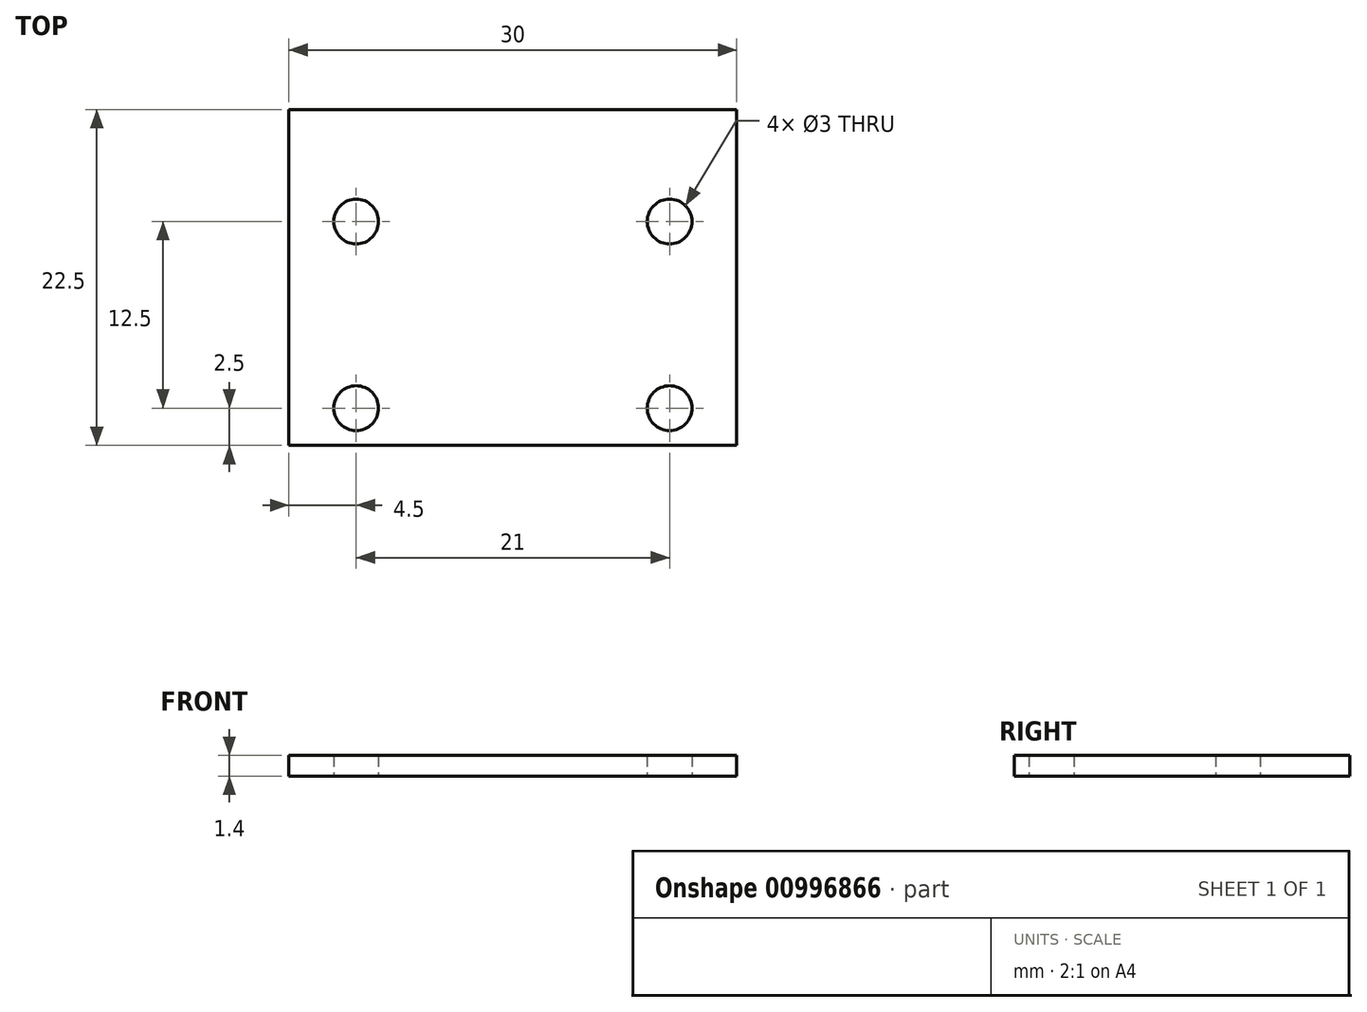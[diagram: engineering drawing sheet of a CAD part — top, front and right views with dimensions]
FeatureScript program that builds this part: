
annotation { "Feature Type Name" : "Feature", "Feature Type Description" : "" }
export const myFeature = defineFeature(function(context is Context, id is Id, definition is map)
    precondition{}
    {
        {
            var Q0;
            Q0=qCreatedBy(makeId("Top.planeOp"),FACE);
            var sketch = newSketch(context, id + "F0", { "sketchPlane" : qUnion([Q0])});
            skLineSegment(sketch, "E0.bottom", {"start": v(-15, 11.25) * mm, "end": v(15, 11.25) * mm});
            skLineSegment(sketch, "E0.top", {"start": v(-15, -11.25) * mm, "end": v(15, -11.25) * mm});
            skLineSegment(sketch, "E0.left", {"start": v(-15, 11.25) * mm, "end": v(-15, -11.25) * mm});
            skLineSegment(sketch, "E0.right", {"start": v(15, 11.25) * mm, "end": v(15, -11.25) * mm});
            skPoint(sketch, "E0.middle", {"position": v(0, 0) * mm});
            skLineSegment(sketch, "E1.bottom", {"start": v(10.5, -8.75) * mm, "end": v(-10.5, -8.75) * mm, "construction": true});
            skLineSegment(sketch, "E1.top", {"start": v(10.5, 3.75) * mm, "end": v(-10.5, 3.75) * mm, "construction": true});
            skLineSegment(sketch, "E1.left", {"start": v(10.5, -8.75) * mm, "end": v(10.5, 3.75) * mm, "construction": true});
            skLineSegment(sketch, "E1.right", {"start": v(-10.5, -8.75) * mm, "end": v(-10.5, 3.75) * mm, "construction": true});
            skPoint(sketch, "E1.middle", {"position": v(0, -2.5) * mm});
            skCircle(sketch, "E2", {"center": v(-10.5, 3.75) * mm, "radius": 1.5 * mm});
            skCircle(sketch, "E3", {"center": v(10.5, 3.75) * mm, "radius": 1.5 * mm});
            skCircle(sketch, "E4", {"center": v(10.5, -8.75) * mm, "radius": 1.5 * mm});
            skCircle(sketch, "E5", {"center": v(-10.5, -8.75) * mm, "radius": 1.5 * mm});
            skSolve(sketch);
        }
        {
            var Q0;
            Q0=makeQuery(id+"F0.imprint","IMPRINT",FACE,{"disambiguationData":[TD([[makeQuery(id+"F0.imprint","IMPRINT",EDGE,{"derivedFrom":sQuery(id+"F0.wireOp",EDGE,"E0.bottom")}),-1.0]])]});
            extrude(context, id + "F1", {"entities" : qUnion([Q0]), "depth" : 1.4 * mm, "offsetDistance" : 25 * mm});
        }
    });
